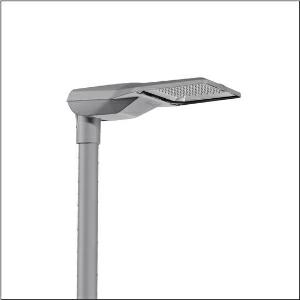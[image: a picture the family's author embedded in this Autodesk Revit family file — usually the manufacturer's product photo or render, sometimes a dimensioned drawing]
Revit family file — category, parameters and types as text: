
# Revit family: streetlight_sl_21_iq_midi___pl52_5xe3h41d08mb_c975
name_source: partatom
category: Lighting Fixtures
units: mm (PartAtom-declared; Revit-internal decimal feet)

## family parameters
Cut with Voids When Loaded = No
Host = Face
Light Source = No
Part Type = Normal
Room Calculation Point = No
Round Connector Dimension = Use Diameter
Shared = No

## types (1)
- --- (1 x LED, 20000 lm, 146.7 W, 4000K)
    Apparent Load = 147 VA
    CIE Flux Codes = 27 59 98 100 100
    Color Rendering = 70
    Color Temperature = 4000K
    Default Elevation = 1800 mm
    Description = Streetlight SL 21 iQ midi, mast luminaire, primary light control with lens, of PMMA, primary optical cover: cover, of toughened safety glass, transparent, light distribution: PL52, light emission: direct distribution, primary light characteristic: asymmetric, installation type: post-top, side-entry, LED, High Power LED, rated luminous flux: 20.000lm, luminous efficacy: 136lm/W, light colour: 740, colour temperature: 4000K, control: Auto-Match, Temp-Guard, Lumen-Switch, Night-Set, Smart-Wire, Light-Fading, Desk-Remote (wireless, voltage-free reading and setting of iQ features in the workshop via application-optimized NFC function/RFID function), optimised constant luminous flux control (CLO 2.0), pre-setting: linear dimming characteristic, mains connection: 230..240V, AC, 50/60Hz, start of lifetime: 147W, end of service life: 161W, reduction: 62W, luminaire housing, of diecast aluminium, powder-coated, Siteco® metallic grey (DB 702S), corrosivity category C5 mid according to DIN EN ISO 12944, please order mast flange separately, inclination adjustable: 0°, 5°, 10°, 15°, sealing non-destructively replaceable, multi-level sealing system, length: 644mm, width: 335mm, height: 110mm, mast flange for spigot size: 42mm (side-entry): 5XC10008XM4, 60/48mm (side-entry/post-top): 5XC10108XM2, 76/60mm (side-entry/post-top): 5XC10108XM1, protection rating (complete): IP66, insulation class (complete): insulation class II (safety insulation), certification: CE, ENEC, ENEC+, VDE, impact resistance: IK09, permissible operating ambient temperature for outdoor applications: -40..+50°C, standard-compliant lighting for roads and squares, packaging unit: 1 piece

Light Distribution: PL52
    Height = 111 mm
    Lamp = 1 x LED
    Lamp Light Flux = 20000 lm
    Lamp Power = 146.7 W
    Lamp count = 1
    Length = 644 mm
    Luminous efficacy = 136 lm/W
    Manufacturer = Siteco
    ModVariant = No
    Model = 5XE3H41D08MB
    Number of Poles = 1
    OnlyDefault = Yes
    Power Factor = 1
    Product Name = Streetlight SL 21 iQ midi | PL52
    Product group = mast luminaire | pylon top
    ProductGroupID = 6100
    Protection Class = Protection class II
    Protection Degree = IP 66
    RLX_Detail_Level = 1
    RLX_Emergency_Light_Flux = 0 lm
    RLX_Emergency_Type = 0
    RLX_Emergency_Type_DB = No
    RlxData = <blob elided: 100569 chars, md5=e9166705>
    Socket = socket
    Standby Power = 0 W
    System Light Flux = 20000 lm
    System Power = 147 W
    Type Comments = factory setting: luminous flux: 100 % | dim-lin: 254 | 753 mA
    Type Image = l_1004298.jpg
    URL = http://relux.com
    VarID = @adj_163273
    Voltage = 0 V
    Weight = 0.00 kg
    Width = 336 mm

## geometry (parser evidence)
native form markers: Blend x4, Sweep x10
no freeform markers — native parametric forms only
